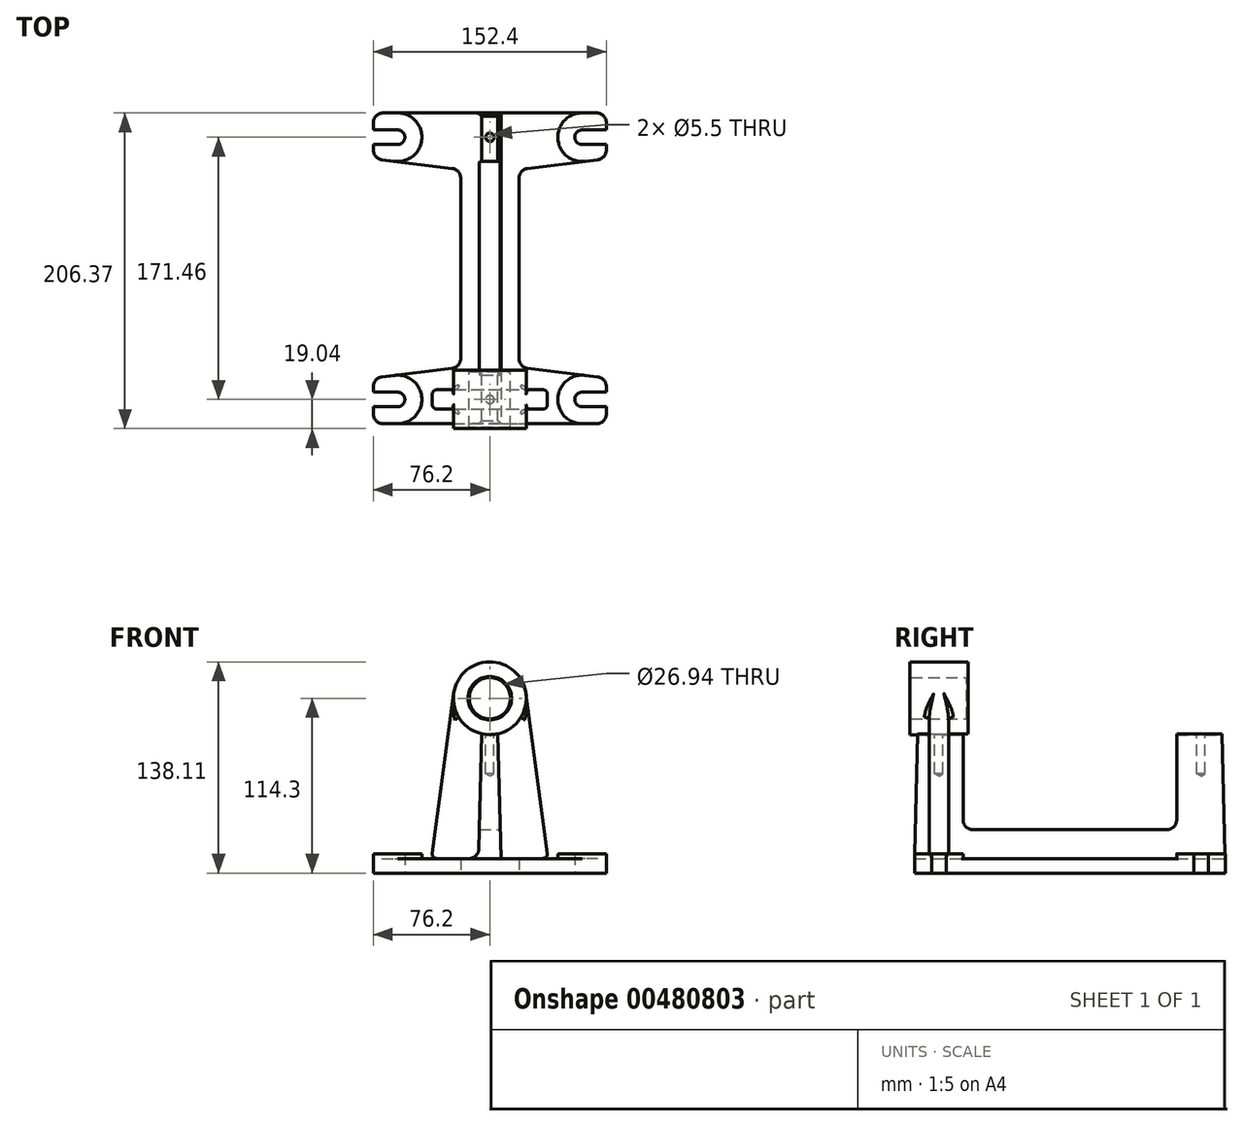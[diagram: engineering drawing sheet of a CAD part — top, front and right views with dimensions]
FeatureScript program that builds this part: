
annotation { "Feature Type Name" : "Feature", "Feature Type Description" : "" }
export const myFeature = defineFeature(function(context is Context, id is Id, definition is map)
    precondition{}
    {
        {
            var Q0;
            Q0=qCreatedBy(makeId("Top.planeOp"),FACE);
            var sketch = newSketch(context, id + "F0", { "sketchPlane" : qUnion([Q0])});
            skLineSegment(sketch, "E0.left", {"start": v(-76.2, 95.25) * mm, "end": v(-76.2, 90.49) * mm});
            skArc(sketch, "E1", {"start": v(-19.05, 59) * mm, "mid": v(-20.64, 63.2) * mm, "end": v(-24.62, 65.3) * mm});
            skLineSegment(sketch, "E2", {"start": v(-70.63, 71) * mm, "end": v(-24.62, 65.3) * mm});
            skArc(sketch, "E3", {"start": v(-60.32, 80.96) * mm, "mid": v(-55.56, 85.72) * mm, "end": v(-60.32, 90.49) * mm});
            skLineSegment(sketch, "E4", {"start": v(-76.2, 90.49) * mm, "end": v(-60.32, 90.49) * mm});
            skLineSegment(sketch, "E5", {"start": v(-60.32, 80.96) * mm, "end": v(-76.2, 80.96) * mm});
            skArc(sketch, "E6.filletArc", {"start": v(-69.85, 101.6) * mm, "mid": v(-74.34, 99.74) * mm, "end": v(-76.2, 95.25) * mm});
            skArc(sketch, "E7.filletArc", {"start": v(-76.2, 77.3) * mm, "mid": v(-74.6, 73.1) * mm, "end": v(-70.63, 71) * mm});
            skLineSegment(sketch, "E8.trimOffspring", {"start": v(-76.2, 80.96) * mm, "end": v(-76.2, 77.3) * mm});
            skLineSegment(sketch, "E9.MirrorCS", {"start": v(76.2, 80.96) * mm, "end": v(76.2, 77.3) * mm});
            skLineSegment(sketch, "E10.MirrorCS", {"start": v(76.2, 95.25) * mm, "end": v(76.2, 90.49) * mm});
            skArc(sketch, "E11.MirrorCS", {"start": v(60.32, 80.96) * mm, "mid": v(55.56, 85.72) * mm, "end": v(60.32, 90.49) * mm});
            skLineSegment(sketch, "E12.MirrorCS", {"start": v(76.2, 90.49) * mm, "end": v(60.32, 90.49) * mm});
            skLineSegment(sketch, "E13.MirrorCS", {"start": v(60.32, 80.96) * mm, "end": v(76.2, 80.96) * mm});
            skArc(sketch, "E14.MirrorCS", {"start": v(69.85, 101.6) * mm, "mid": v(74.34, 99.74) * mm, "end": v(76.2, 95.25) * mm});
            skArc(sketch, "E15.MirrorCS", {"start": v(19.05, 59) * mm, "mid": v(20.64, 63.2) * mm, "end": v(24.62, 65.3) * mm});
            skLineSegment(sketch, "E16.MirrorCS", {"start": v(70.63, 71) * mm, "end": v(24.62, 65.3) * mm});
            skArc(sketch, "E17.MirrorCS", {"start": v(76.2, 77.3) * mm, "mid": v(74.6, 73.1) * mm, "end": v(70.63, 71) * mm});
            skLineSegment(sketch, "E18.MirrorCS", {"start": v(-76.2, -95.25) * mm, "end": v(-76.2, -90.49) * mm});
            skLineSegment(sketch, "E19.MirrorCS", {"start": v(-76.2, -80.96) * mm, "end": v(-76.2, -77.3) * mm});
            skLineSegment(sketch, "E20.MirrorCS", {"start": v(76.2, -95.25) * mm, "end": v(76.2, -90.49) * mm});
            skLineSegment(sketch, "E21.MirrorCS", {"start": v(76.2, -80.96) * mm, "end": v(76.2, -77.3) * mm});
            skArc(sketch, "E22.MirrorCS", {"start": v(-19.05, -59) * mm, "mid": v(-20.64, -63.2) * mm, "end": v(-24.62, -65.3) * mm});
            skArc(sketch, "E23.MirrorCS", {"start": v(-76.2, -77.3) * mm, "mid": v(-74.6, -73.1) * mm, "end": v(-70.63, -71) * mm});
            skLineSegment(sketch, "E24.MirrorCS", {"start": v(-70.63, -71) * mm, "end": v(-24.62, -65.3) * mm});
            skArc(sketch, "E25.MirrorCS", {"start": v(19.05, -59) * mm, "mid": v(20.64, -63.2) * mm, "end": v(24.62, -65.3) * mm});
            skArc(sketch, "E26.MirrorCS", {"start": v(69.85, -101.6) * mm, "mid": v(74.34, -99.74) * mm, "end": v(76.2, -95.25) * mm});
            skLineSegment(sketch, "E27.MirrorCS", {"start": v(60.32, -80.96) * mm, "end": v(76.2, -80.96) * mm});
            skArc(sketch, "E28.MirrorCS", {"start": v(-69.85, -101.6) * mm, "mid": v(-74.34, -99.74) * mm, "end": v(-76.2, -95.25) * mm});
            skLineSegment(sketch, "E29.MirrorCS", {"start": v(-76.2, -90.49) * mm, "end": v(-60.32, -90.49) * mm});
            skArc(sketch, "E30.MirrorCS", {"start": v(-60.32, -80.96) * mm, "mid": v(-55.56, -85.72) * mm, "end": v(-60.32, -90.49) * mm});
            skArc(sketch, "E31.MirrorCS", {"start": v(76.2, -77.3) * mm, "mid": v(74.6, -73.1) * mm, "end": v(70.63, -71) * mm});
            skLineSegment(sketch, "E32.MirrorCS", {"start": v(76.2, -90.49) * mm, "end": v(60.32, -90.49) * mm});
            skLineSegment(sketch, "E33.MirrorCS", {"start": v(-60.32, -80.96) * mm, "end": v(-76.2, -80.96) * mm});
            skLineSegment(sketch, "E34.MirrorCS", {"start": v(70.63, -71) * mm, "end": v(24.62, -65.3) * mm});
            skArc(sketch, "E35.MirrorCS", {"start": v(60.32, -80.96) * mm, "mid": v(55.56, -85.72) * mm, "end": v(60.32, -90.49) * mm});
            skLineSegment(sketch, "E36", {"start": v(-69.85, 101.6) * mm, "end": v(69.85, 101.6) * mm});
            skLineSegment(sketch, "E37", {"start": v(-19.05, 59) * mm, "end": v(-19.05, -59) * mm});
            skLineSegment(sketch, "E38", {"start": v(19.05, 59) * mm, "end": v(19.05, -59) * mm});
            skLineSegment(sketch, "E39", {"start": v(-69.85, -101.6) * mm, "end": v(69.85, -101.6) * mm});
            skSolve(sketch);
        }
        {
            var Q0;
            Q0=makeQuery(id+"F0.imprint","IMPRINT",FACE,{"disambiguationData":[TD([[makeQuery(id+"F0.imprint","IMPRINT",EDGE,{"derivedFrom":sQuery(id+"F0.wireOp",EDGE,"E0.left")}),1.0]])]});
            extrude(context, id + "F1", {"entities" : qUnion([Q0]), "depth" : 9.52 * mm});
        }
        {
            var Q0;
            Q0=makeQuery(id+"F1.opExtrude","CAP_FACE",FACE,{"disambiguationData":[OSD([sQuery(id+"F0.wireOp",EDGE,"E0.left"),sQuery(id+"F0.wireOp",EDGE,"E1"),sQuery(id+"F0.wireOp",EDGE,"E2"),sQuery(id+"F0.wireOp",EDGE,"E3"),sQuery(id+"F0.wireOp",EDGE,"E4"),sQuery(id+"F0.wireOp",EDGE,"E5"),sQuery(id+"F0.wireOp",EDGE,"E6.filletArc"),sQuery(id+"F0.wireOp",EDGE,"E7.filletArc"),sQuery(id+"F0.wireOp",EDGE,"E8.trimOffspring"),sQuery(id+"F0.wireOp",EDGE,"E9.MirrorCS"),sQuery(id+"F0.wireOp",EDGE,"E10.MirrorCS"),sQuery(id+"F0.wireOp",EDGE,"E11.MirrorCS"),sQuery(id+"F0.wireOp",EDGE,"E12.MirrorCS"),sQuery(id+"F0.wireOp",EDGE,"E13.MirrorCS"),sQuery(id+"F0.wireOp",EDGE,"E14.MirrorCS"),sQuery(id+"F0.wireOp",EDGE,"E15.MirrorCS"),sQuery(id+"F0.wireOp",EDGE,"E16.MirrorCS"),sQuery(id+"F0.wireOp",EDGE,"E17.MirrorCS"),sQuery(id+"F0.wireOp",EDGE,"E18.MirrorCS"),sQuery(id+"F0.wireOp",EDGE,"E19.MirrorCS"),sQuery(id+"F0.wireOp",EDGE,"E20.MirrorCS"),sQuery(id+"F0.wireOp",EDGE,"E21.MirrorCS"),sQuery(id+"F0.wireOp",EDGE,"E22.MirrorCS"),sQuery(id+"F0.wireOp",EDGE,"E23.MirrorCS"),sQuery(id+"F0.wireOp",EDGE,"E24.MirrorCS"),sQuery(id+"F0.wireOp",EDGE,"E25.MirrorCS"),sQuery(id+"F0.wireOp",EDGE,"E26.MirrorCS"),sQuery(id+"F0.wireOp",EDGE,"E27.MirrorCS"),sQuery(id+"F0.wireOp",EDGE,"E28.MirrorCS"),sQuery(id+"F0.wireOp",EDGE,"E29.MirrorCS"),sQuery(id+"F0.wireOp",EDGE,"E30.MirrorCS"),sQuery(id+"F0.wireOp",EDGE,"E31.MirrorCS"),sQuery(id+"F0.wireOp",EDGE,"E32.MirrorCS"),sQuery(id+"F0.wireOp",EDGE,"E33.MirrorCS"),sQuery(id+"F0.wireOp",EDGE,"E34.MirrorCS"),sQuery(id+"F0.wireOp",EDGE,"E35.MirrorCS"),sQuery(id+"F0.wireOp",EDGE,"E36"),sQuery(id+"F0.wireOp",EDGE,"E37"),sQuery(id+"F0.wireOp",EDGE,"E38"),sQuery(id+"F0.wireOp",EDGE,"E39")])],"isStart":false});
            var sketch = newSketch(context, id + "F2", { "sketchPlane" : qUnion([Q0])});
            skArc(sketch, "E40", {"start": v(-62.28, 69.97) * mm, "mid": v(-44.48, 84.75) * mm, "end": v(-60.32, 101.6) * mm});
            skLineSegment(sketch, "E41.0", {"start": v(-69.85, 101.6) * mm, "end": v(-60.32, 101.6) * mm});
            skArc(sketch, "E42.0", {"start": v(-69.85, 101.6) * mm, "mid": v(-74.34, 99.74) * mm, "end": v(-76.2, 95.25) * mm});
            skLineSegment(sketch, "E43.0", {"start": v(-76.2, 95.25) * mm, "end": v(-76.2, 90.49) * mm});
            skLineSegment(sketch, "E44.0", {"start": v(-76.2, 80.96) * mm, "end": v(-76.2, 77.3) * mm});
            skArc(sketch, "E45.0", {"start": v(-76.2, 77.3) * mm, "mid": v(-74.6, 73.1) * mm, "end": v(-70.63, 71) * mm});
            skLineSegment(sketch, "E46.0", {"start": v(-70.63, 71) * mm, "end": v(-62.28, 69.97) * mm});
            skLineSegment(sketch, "E47.0", {"start": v(-76.2, 90.49) * mm, "end": v(-60.32, 90.49) * mm});
            skArc(sketch, "E48.0", {"start": v(-60.32, 80.96) * mm, "mid": v(-55.56, 85.72) * mm, "end": v(-60.32, 90.49) * mm});
            skLineSegment(sketch, "E49.0", {"start": v(-60.32, 80.96) * mm, "end": v(-76.2, 80.96) * mm});
            skLineSegment(sketch, "E50.MirrorCS", {"start": v(76.2, 80.96) * mm, "end": v(76.2, 77.3) * mm});
            skLineSegment(sketch, "E51.MirrorCS", {"start": v(76.2, 95.25) * mm, "end": v(76.2, 90.49) * mm});
            skLineSegment(sketch, "E52.MirrorCS", {"start": v(70.63, 71) * mm, "end": v(62.28, 69.97) * mm});
            skLineSegment(sketch, "E53.MirrorCS", {"start": v(76.2, 90.49) * mm, "end": v(60.32, 90.49) * mm});
            skArc(sketch, "E54.MirrorCS", {"start": v(76.2, 77.3) * mm, "mid": v(74.6, 73.1) * mm, "end": v(70.63, 71) * mm});
            skArc(sketch, "E55.MirrorCS", {"start": v(60.32, 80.96) * mm, "mid": v(55.56, 85.72) * mm, "end": v(60.32, 90.49) * mm});
            skLineSegment(sketch, "E56.MirrorCS", {"start": v(60.32, 80.96) * mm, "end": v(76.2, 80.96) * mm});
            skArc(sketch, "E57.MirrorCS", {"start": v(69.85, 101.6) * mm, "mid": v(74.34, 99.74) * mm, "end": v(76.2, 95.25) * mm});
            skLineSegment(sketch, "E58.MirrorCS", {"start": v(69.85, 101.6) * mm, "end": v(60.32, 101.6) * mm});
            skArc(sketch, "E59.MirrorCS", {"start": v(62.28, 69.97) * mm, "mid": v(44.48, 84.75) * mm, "end": v(60.32, 101.6) * mm});
            skLineSegment(sketch, "E60.MirrorCS", {"start": v(-76.2, -80.96) * mm, "end": v(-76.2, -77.3) * mm});
            skLineSegment(sketch, "E61.MirrorCS", {"start": v(-76.2, -95.25) * mm, "end": v(-76.2, -90.49) * mm});
            skLineSegment(sketch, "E62.MirrorCS", {"start": v(76.2, -80.96) * mm, "end": v(76.2, -77.3) * mm});
            skLineSegment(sketch, "E63.MirrorCS", {"start": v(76.2, -95.25) * mm, "end": v(76.2, -90.49) * mm});
            skLineSegment(sketch, "E64.MirrorCS", {"start": v(-70.63, -71) * mm, "end": v(-62.28, -69.97) * mm});
            skArc(sketch, "E65.MirrorCS", {"start": v(-76.2, -77.3) * mm, "mid": v(-74.6, -73.1) * mm, "end": v(-70.63, -71) * mm});
            skArc(sketch, "E66.MirrorCS", {"start": v(-69.85, -101.6) * mm, "mid": v(-74.34, -99.74) * mm, "end": v(-76.2, -95.25) * mm});
            skLineSegment(sketch, "E67.MirrorCS", {"start": v(-69.85, -101.6) * mm, "end": v(-60.32, -101.6) * mm});
            skArc(sketch, "E68.MirrorCS", {"start": v(-62.28, -69.97) * mm, "mid": v(-44.48, -84.75) * mm, "end": v(-60.32, -101.6) * mm});
            skArc(sketch, "E69.MirrorCS", {"start": v(60.32, -80.96) * mm, "mid": v(55.56, -85.72) * mm, "end": v(60.32, -90.49) * mm});
            skArc(sketch, "E70.MirrorCS", {"start": v(76.2, -77.3) * mm, "mid": v(74.6, -73.1) * mm, "end": v(70.63, -71) * mm});
            skLineSegment(sketch, "E71.MirrorCS", {"start": v(76.2, -90.49) * mm, "end": v(60.32, -90.49) * mm});
            skLineSegment(sketch, "E72.MirrorCS", {"start": v(-76.2, -90.49) * mm, "end": v(-60.32, -90.49) * mm});
            skArc(sketch, "E73.MirrorCS", {"start": v(-60.32, -80.96) * mm, "mid": v(-55.56, -85.72) * mm, "end": v(-60.32, -90.49) * mm});
            skLineSegment(sketch, "E74.MirrorCS", {"start": v(-60.32, -80.96) * mm, "end": v(-76.2, -80.96) * mm});
            skLineSegment(sketch, "E75.MirrorCS", {"start": v(70.63, -71) * mm, "end": v(62.28, -69.97) * mm});
            skArc(sketch, "E76.MirrorCS", {"start": v(69.85, -101.6) * mm, "mid": v(74.34, -99.74) * mm, "end": v(76.2, -95.25) * mm});
            skArc(sketch, "E77.MirrorCS", {"start": v(62.28, -69.97) * mm, "mid": v(44.48, -84.75) * mm, "end": v(60.32, -101.6) * mm});
            skLineSegment(sketch, "E78.MirrorCS", {"start": v(60.32, -80.96) * mm, "end": v(76.2, -80.96) * mm});
            skLineSegment(sketch, "E79.MirrorCS", {"start": v(69.85, -101.6) * mm, "end": v(60.32, -101.6) * mm});
            skSolve(sketch);
        }
        {
            var Q0;
            Q0=makeQuery(id+"F2.imprint","IMPRINT",FACE,{"disambiguationData":[TD([[makeQuery(id+"F2.imprint","IMPRINT",EDGE,{"derivedFrom":sQuery(id+"F2.wireOp",EDGE,"E60.MirrorCS")}),-1.0]])]});
            var Q1;
            Q1=makeQuery(id+"F2.imprint","IMPRINT",FACE,{"disambiguationData":[TD([[makeQuery(id+"F2.imprint","IMPRINT",EDGE,{"derivedFrom":sQuery(id+"F2.wireOp",EDGE,"E62.MirrorCS")}),1.0]])]});
            var Q2;
            Q2=makeQuery(id+"F2.imprint","IMPRINT",FACE,{"disambiguationData":[TD([[makeQuery(id+"F2.imprint","IMPRINT",EDGE,{"derivedFrom":sQuery(id+"F2.wireOp",EDGE,"E40")}),1.0]])]});
            var Q3;
            Q3=makeQuery(id+"F2.imprint","IMPRINT",FACE,{"disambiguationData":[TD([[makeQuery(id+"F2.imprint","IMPRINT",EDGE,{"derivedFrom":sQuery(id+"F2.wireOp",EDGE,"E50.MirrorCS")}),-1.0]])]});
            extrude(context, id + "F3", {"entities" : qUnion([Q0, Q1, Q2, Q3]), "operationType" : NewBodyOperationType.ADD, "depth" : 3.17 * mm});
        }
        {
            var Q0;
            Q0=makeQuery(id+"F3.boolean.opBoolean","MERGE",FACE,{"derivedFrom":[makeQuery(id+"F1.opExtrude","SWEPT_FACE",FACE,{"disambiguationData":[OSD([sQuery(id+"F0.wireOp",EDGE,"E39")])]}),makeQuery(id+"F3.opExtrude","SWEPT_FACE",FACE,{"disambiguationData":[OSD([sQuery(id+"F2.wireOp",EDGE,"E67.MirrorCS")])]}),makeQuery(id+"F3.opExtrude","SWEPT_FACE",FACE,{"disambiguationData":[OSD([sQuery(id+"F2.wireOp",EDGE,"E79.MirrorCS")])]})]});
            cPlane(context, id + "F4", {"entities" : qUnion([Q0]), "cplaneType" : CPlaneType.OFFSET, "offset" : 15.88 * mm, "oppositeDirection" : true, "width" : 152.4 * mm, "height" : 152.4 * mm});
        }
        {
            var Q0;
            Q0=qCreatedBy(id+"F4.planeOp",FACE);
            var sketch = newSketch(context, id + "F5", { "sketchPlane" : qUnion([Q0])});
            skCircle(sketch, "E80", {"center": v(0, 114.3) * mm, "radius": 23.81 * mm});
            skCircle(sketch, "E81", {"center": v(0, 114.3) * mm, "radius": 13.47 * mm});
            skSolve(sketch);
        }
        {
            var Q0;
            Q0=makeQuery(id+"F5.imprint","IMPRINT",FACE,{"disambiguationData":[TD([[makeQuery(id+"F5.imprint","IMPRINT",EDGE,{"derivedFrom":sQuery(id+"F5.wireOp",EDGE,"E80")}),1.0]])]});
            extrude(context, id + "F6", {"entities" : qUnion([Q0]), "endBound" : BoundingType.SYMMETRIC, "depth" : 38.1 * mm});
        }
        {
            var Q0;
            Q0=qCreatedBy(id+"F4.planeOp",FACE);
            var sketch = newSketch(context, id + "F7", { "sketchPlane" : qUnion([Q0])});
            skLineSegment(sketch, "E82", {"start": v(-23.6, 117.47) * mm, "end": v(-38.1, 9.52) * mm});
            skLineSegment(sketch, "E83", {"start": v(38.1, 9.52) * mm, "end": v(23.6, 117.47) * mm});
            skArc(sketch, "E84.0", {"start": v(-23.6, 117.47) * mm, "mid": v(0, 90.49) * mm, "end": v(23.6, 117.47) * mm});
            skLineSegment(sketch, "E85.0", {"start": v(-38.1, 9.53) * mm, "end": v(38.1, 9.53) * mm});
            skSolve(sketch);
        }
        {
            var Q0;
            Q0=makeQuery(id+"F7.imprint","IMPRINT",FACE,{"disambiguationData":[TD([[makeQuery(id+"F7.imprint","IMPRINT",EDGE,{"derivedFrom":sQuery(id+"F7.wireOp",EDGE,"E82")}),1.0]])]});
            extrude(context, id + "F8", {"entities" : qUnion([Q0]), "operationType" : NewBodyOperationType.ADD, "endBound" : BoundingType.SYMMETRIC, "depth" : 12.7 * mm});
        }
        {
            var Q0;
            Q0=makeQuery(id+"F1.opExtrude","CAP_FACE",FACE,{"disambiguationData":[OSD([sQuery(id+"F0.wireOp",EDGE,"E0.left"),sQuery(id+"F0.wireOp",EDGE,"E1"),sQuery(id+"F0.wireOp",EDGE,"E2"),sQuery(id+"F0.wireOp",EDGE,"E3"),sQuery(id+"F0.wireOp",EDGE,"E4"),sQuery(id+"F0.wireOp",EDGE,"E5"),sQuery(id+"F0.wireOp",EDGE,"E6.filletArc"),sQuery(id+"F0.wireOp",EDGE,"E7.filletArc"),sQuery(id+"F0.wireOp",EDGE,"E8.trimOffspring"),sQuery(id+"F0.wireOp",EDGE,"E9.MirrorCS"),sQuery(id+"F0.wireOp",EDGE,"E10.MirrorCS"),sQuery(id+"F0.wireOp",EDGE,"E11.MirrorCS"),sQuery(id+"F0.wireOp",EDGE,"E12.MirrorCS"),sQuery(id+"F0.wireOp",EDGE,"E13.MirrorCS"),sQuery(id+"F0.wireOp",EDGE,"E14.MirrorCS"),sQuery(id+"F0.wireOp",EDGE,"E15.MirrorCS"),sQuery(id+"F0.wireOp",EDGE,"E16.MirrorCS"),sQuery(id+"F0.wireOp",EDGE,"E17.MirrorCS"),sQuery(id+"F0.wireOp",EDGE,"E18.MirrorCS"),sQuery(id+"F0.wireOp",EDGE,"E19.MirrorCS"),sQuery(id+"F0.wireOp",EDGE,"E20.MirrorCS"),sQuery(id+"F0.wireOp",EDGE,"E21.MirrorCS"),sQuery(id+"F0.wireOp",EDGE,"E22.MirrorCS"),sQuery(id+"F0.wireOp",EDGE,"E23.MirrorCS"),sQuery(id+"F0.wireOp",EDGE,"E24.MirrorCS"),sQuery(id+"F0.wireOp",EDGE,"E25.MirrorCS"),sQuery(id+"F0.wireOp",EDGE,"E26.MirrorCS"),sQuery(id+"F0.wireOp",EDGE,"E27.MirrorCS"),sQuery(id+"F0.wireOp",EDGE,"E28.MirrorCS"),sQuery(id+"F0.wireOp",EDGE,"E29.MirrorCS"),sQuery(id+"F0.wireOp",EDGE,"E30.MirrorCS"),sQuery(id+"F0.wireOp",EDGE,"E31.MirrorCS"),sQuery(id+"F0.wireOp",EDGE,"E32.MirrorCS"),sQuery(id+"F0.wireOp",EDGE,"E33.MirrorCS"),sQuery(id+"F0.wireOp",EDGE,"E34.MirrorCS"),sQuery(id+"F0.wireOp",EDGE,"E35.MirrorCS"),sQuery(id+"F0.wireOp",EDGE,"E36"),sQuery(id+"F0.wireOp",EDGE,"E37"),sQuery(id+"F0.wireOp",EDGE,"E38"),sQuery(id+"F0.wireOp",EDGE,"E39")])],"isStart":false});
            var sketch = newSketch(context, id + "F9", { "sketchPlane" : qUnion([Q0])});
            skLineSegment(sketch, "E86.left", {"start": v(-7.35, 101.6) * mm, "end": v(-7.35, -101.6) * mm});
            skLineSegment(sketch, "E86.right", {"start": v(7.35, 101.6) * mm, "end": v(7.35, -101.6) * mm});
            skLineSegment(sketch, "E87", {"start": v(7.35, -101.6) * mm, "end": v(-7.35, -101.6) * mm});
            skLineSegment(sketch, "E88", {"start": v(-7.35, 101.6) * mm, "end": v(7.35, 101.6) * mm});
            skSolve(sketch);
        }
        {
            var Q0;
            Q0=makeQuery(id+"F9.imprint","IMPRINT",FACE,{"disambiguationData":[TD([[makeQuery(id+"F9.imprint","IMPRINT",EDGE,{"derivedFrom":sQuery(id+"F9.wireOp",EDGE,"E86.left")}),1.0]])]});
            var Q1;
            Q1=makeQuery(id+"F6.opExtrude","SWEPT_FACE",FACE,{"disambiguationData":[OSD([sQuery(id+"F5.wireOp",EDGE,"E80")])]});
            extrude(context, id + "F10", {"entities" : qUnion([Q0]), "endBound" : BoundingType.UP_TO_SURFACE, "endBoundEntityFace" : qUnion([Q1]), "depth" : 25.4 * mm, "hasDraft" : true, "draftAngle" : 1.5 * degree, "draftPullDirection" : true});
        }
        {
            var Q0;
            Q0=qCreatedBy(makeId("Right.planeOp"),FACE);
            var sketch = newSketch(context, id + "F11", { "sketchPlane" : qUnion([Q0])});
            skLineSegment(sketch, "E89.MirrorCS", {"start": v(69.85, 91.1) * mm, "end": v(69.85, 34.77) * mm});
            skLineSegment(sketch, "E90.MirrorCS", {"start": v(-69.85, 91.1) * mm, "end": v(-69.85, 34.77) * mm});
            skLineSegment(sketch, "E91.0", {"start": v(63.5, 28.42) * mm, "end": v(-63.5, 28.42) * mm});
            skPoint(sketch, "E92.newPointA", {"position": v(69.85, 9.52) * mm});
            skArc(sketch, "E92.filletArc", {"start": v(63.5, 28.42) * mm, "mid": v(68, 30.28) * mm, "end": v(69.85, 34.77) * mm});
            skPoint(sketch, "E93.newPointB", {"position": v(-69.85, 9.52) * mm});
            skArc(sketch, "E93.filletArc", {"start": v(-69.85, 34.77) * mm, "mid": v(-68, 30.28) * mm, "end": v(-63.5, 28.42) * mm});
            skLineSegment(sketch, "E94", {"start": v(69.85, 91.1) * mm, "end": v(-69.85, 91.1) * mm});
            skSolve(sketch);
        }
        {
            var Q0;
            Q0=makeQuery(id+"F11.imprint","IMPRINT",FACE,{"disambiguationData":[TD([[makeQuery(id+"F11.imprint","IMPRINT",EDGE,{"derivedFrom":sQuery(id+"F11.wireOp",EDGE,"E89.MirrorCS")}),-1.0]])]});
            extrude(context, id + "F12", {"entities" : qUnion([Q0]), "operationType" : NewBodyOperationType.REMOVE, "endBound" : BoundingType.SYMMETRIC, "oppositeDirection" : true, "depth" : 50.8 * mm});
        }
        {
            var Q0;
            Q0=makeQuery(id+"F10.opExtrude","SWEPT_BODY",BODY,{"disambiguationData":[OSD([sQuery(id+"F9.wireOp",EDGE,"E86.left"),sQuery(id+"F9.wireOp",EDGE,"E86.right"),sQuery(id+"F9.wireOp",EDGE,"E87"),sQuery(id+"F9.wireOp",EDGE,"E88")])]});
            var Q1;
            Q1=makeQuery(id+"F1.opExtrude","SWEPT_BODY",BODY,{"disambiguationData":[OSD([sQuery(id+"F0.wireOp",EDGE,"E0.left"),sQuery(id+"F0.wireOp",EDGE,"E1"),sQuery(id+"F0.wireOp",EDGE,"E2"),sQuery(id+"F0.wireOp",EDGE,"E3"),sQuery(id+"F0.wireOp",EDGE,"E4"),sQuery(id+"F0.wireOp",EDGE,"E5"),sQuery(id+"F0.wireOp",EDGE,"E6.filletArc"),sQuery(id+"F0.wireOp",EDGE,"E7.filletArc"),sQuery(id+"F0.wireOp",EDGE,"E8.trimOffspring"),sQuery(id+"F0.wireOp",EDGE,"E9.MirrorCS"),sQuery(id+"F0.wireOp",EDGE,"E10.MirrorCS"),sQuery(id+"F0.wireOp",EDGE,"E11.MirrorCS"),sQuery(id+"F0.wireOp",EDGE,"E12.MirrorCS"),sQuery(id+"F0.wireOp",EDGE,"E13.MirrorCS"),sQuery(id+"F0.wireOp",EDGE,"E14.MirrorCS"),sQuery(id+"F0.wireOp",EDGE,"E15.MirrorCS"),sQuery(id+"F0.wireOp",EDGE,"E16.MirrorCS"),sQuery(id+"F0.wireOp",EDGE,"E17.MirrorCS"),sQuery(id+"F0.wireOp",EDGE,"E18.MirrorCS"),sQuery(id+"F0.wireOp",EDGE,"E19.MirrorCS"),sQuery(id+"F0.wireOp",EDGE,"E20.MirrorCS"),sQuery(id+"F0.wireOp",EDGE,"E21.MirrorCS"),sQuery(id+"F0.wireOp",EDGE,"E22.MirrorCS"),sQuery(id+"F0.wireOp",EDGE,"E23.MirrorCS"),sQuery(id+"F0.wireOp",EDGE,"E24.MirrorCS"),sQuery(id+"F0.wireOp",EDGE,"E25.MirrorCS"),sQuery(id+"F0.wireOp",EDGE,"E26.MirrorCS"),sQuery(id+"F0.wireOp",EDGE,"E27.MirrorCS"),sQuery(id+"F0.wireOp",EDGE,"E28.MirrorCS"),sQuery(id+"F0.wireOp",EDGE,"E29.MirrorCS"),sQuery(id+"F0.wireOp",EDGE,"E30.MirrorCS"),sQuery(id+"F0.wireOp",EDGE,"E31.MirrorCS"),sQuery(id+"F0.wireOp",EDGE,"E32.MirrorCS"),sQuery(id+"F0.wireOp",EDGE,"E33.MirrorCS"),sQuery(id+"F0.wireOp",EDGE,"E34.MirrorCS"),sQuery(id+"F0.wireOp",EDGE,"E35.MirrorCS"),sQuery(id+"F0.wireOp",EDGE,"E36"),sQuery(id+"F0.wireOp",EDGE,"E37"),sQuery(id+"F0.wireOp",EDGE,"E38"),sQuery(id+"F0.wireOp",EDGE,"E39")])]});
            booleanBodies(context, id + "F13", {"operationType" : BooleanOperationType.UNION, "tools" : qUnion([Q0, Q1])});
        }
        {
            var Q0;
            {var subQ0=sQuery(id+"F7.wireOp",EDGE,"E85.0");var subQ1=sQuery(id+"F7.wireOp",EDGE,"E84.0");var subQ2=sQuery(id+"F7.wireOp",EDGE,"E83");var subQ3=sQuery(id+"F7.wireOp",EDGE,"E82");var subQ4=sQuery(id+"F9.wireOp",EDGE,"E86.right");Q0=makeQuery(id+"F13.opBoolean","SPLIT",EDGE,{"disambiguationData":[TD([makeQuery(id+"F8.opExtrude","CAP_FACE",FACE,{"disambiguationData":[OSD([subQ3,subQ2,subQ1,subQ0])],"isStart":true})])],"derivedFrom":makeQuery(id+"F10.opExtrude","CAP_EDGE",EDGE,{"disambiguationData":[OSD([subQ4])],"isStart":true})});}
            var Q1;
            {var subQ0=sQuery(id+"F9.wireOp",EDGE,"E86.left");var subQ1=sQuery(id+"F7.wireOp",EDGE,"E85.0");var subQ2=sQuery(id+"F7.wireOp",EDGE,"E84.0");var subQ3=sQuery(id+"F7.wireOp",EDGE,"E83");var subQ4=sQuery(id+"F7.wireOp",EDGE,"E82");Q1=makeQuery(id+"F13.opBoolean","SPLIT",EDGE,{"disambiguationData":[TD([makeQuery(id+"F8.opExtrude","CAP_FACE",FACE,{"disambiguationData":[OSD([subQ4,subQ3,subQ2,subQ1])],"isStart":true})])],"derivedFrom":makeQuery(id+"F10.opExtrude","CAP_EDGE",EDGE,{"disambiguationData":[OSD([subQ0])],"isStart":true})});}
            fillet(context, id + "F14", {"entities" : qUnion([Q0, Q1]), "radius" : 6.35 * mm, "tangentPropagation" : true, "allowEdgeOverflow" : false});
        }
        {
            var Q0;
            {var subQ0=sQuery(id+"F9.wireOp",EDGE,"E86.left");var subQ1=sQuery(id+"F0.wireOp",EDGE,"E39");Q0=makeQuery(id+"F13.opBoolean","SPLIT",EDGE,{"disambiguationData":[TD([makeQuery(id+"F1.opExtrude","SWEPT_FACE",FACE,{"disambiguationData":[OSD([subQ1])]})])],"derivedFrom":makeQuery(id+"F10.opExtrude","CAP_EDGE",EDGE,{"disambiguationData":[OSD([subQ0])],"isStart":true})});}
            var Q1;
            {var subQ0=sQuery(id+"F0.wireOp",EDGE,"E39");var subQ1=sQuery(id+"F9.wireOp",EDGE,"E86.right");Q1=makeQuery(id+"F13.opBoolean","SPLIT",EDGE,{"disambiguationData":[TD([makeQuery(id+"F1.opExtrude","SWEPT_FACE",FACE,{"disambiguationData":[OSD([subQ0])]})])],"derivedFrom":makeQuery(id+"F10.opExtrude","CAP_EDGE",EDGE,{"disambiguationData":[OSD([subQ1])],"isStart":true})});}
            var Q2;
            {var subQ0=sQuery(id+"F0.wireOp",EDGE,"E36");var subQ1=sQuery(id+"F9.wireOp",EDGE,"E86.right");Q2=makeQuery(id+"F13.opBoolean","SPLIT",EDGE,{"disambiguationData":[TD([makeQuery(id+"F1.opExtrude","SWEPT_FACE",FACE,{"disambiguationData":[OSD([subQ0])]})])],"derivedFrom":makeQuery(id+"F10.opExtrude","CAP_EDGE",EDGE,{"disambiguationData":[OSD([subQ1])],"isStart":true})});}
            var Q3;
            {var subQ0=sQuery(id+"F9.wireOp",EDGE,"E86.left");var subQ1=sQuery(id+"F0.wireOp",EDGE,"E36");Q3=makeQuery(id+"F13.opBoolean","SPLIT",EDGE,{"disambiguationData":[TD([makeQuery(id+"F1.opExtrude","SWEPT_FACE",FACE,{"disambiguationData":[OSD([subQ1])]})])],"derivedFrom":makeQuery(id+"F10.opExtrude","CAP_EDGE",EDGE,{"disambiguationData":[OSD([subQ0])],"isStart":true})});}
            var Q4;
            {var subQ0=sQuery(id+"F7.wireOp",EDGE,"E82");Q4=makeQuery(id+"F13.opBoolean","SPLIT",FACE,{"disambiguationData":[TD([makeQuery(id+"F8.opExtrude","SWEPT_FACE",FACE,{"disambiguationData":[OSD([subQ0])]})])],"derivedFrom":makeQuery(id+"F8.opExtrude","CAP_FACE",FACE,{"disambiguationData":[OSD([subQ0,sQuery(id+"F7.wireOp",EDGE,"E83"),sQuery(id+"F7.wireOp",EDGE,"E84.0"),sQuery(id+"F7.wireOp",EDGE,"E85.0")])],"isStart":true})});}
            var Q5;
            {var subQ0=sQuery(id+"F7.wireOp",EDGE,"E83");Q5=makeQuery(id+"F13.opBoolean","SPLIT",FACE,{"disambiguationData":[TD([makeQuery(id+"F8.opExtrude","SWEPT_FACE",FACE,{"disambiguationData":[OSD([subQ0])]})])],"derivedFrom":makeQuery(id+"F8.opExtrude","CAP_FACE",FACE,{"disambiguationData":[OSD([sQuery(id+"F7.wireOp",EDGE,"E82"),subQ0,sQuery(id+"F7.wireOp",EDGE,"E84.0"),sQuery(id+"F7.wireOp",EDGE,"E85.0")])],"isStart":true})});}
            var Q6;
            Q6=makeQuery(id+"F8.opExtrude","SWEPT_FACE",FACE,{"disambiguationData":[OSD([sQuery(id+"F7.wireOp",EDGE,"E83")])]});
            var Q7;
            {var subQ0=sQuery(id+"F7.wireOp",EDGE,"E83");Q7=makeQuery(id+"F13.opBoolean","SPLIT",FACE,{"disambiguationData":[TD([makeQuery(id+"F8.opExtrude","SWEPT_FACE",FACE,{"disambiguationData":[OSD([subQ0])]})])],"derivedFrom":makeQuery(id+"F8.opExtrude","CAP_FACE",FACE,{"disambiguationData":[OSD([sQuery(id+"F7.wireOp",EDGE,"E82"),subQ0,sQuery(id+"F7.wireOp",EDGE,"E84.0"),sQuery(id+"F7.wireOp",EDGE,"E85.0")])],"isStart":false})});}
            var Q8;
            {var subQ0=sQuery(id+"F7.wireOp",EDGE,"E82");Q8=makeQuery(id+"F13.opBoolean","SPLIT",FACE,{"disambiguationData":[TD([makeQuery(id+"F8.opExtrude","SWEPT_FACE",FACE,{"disambiguationData":[OSD([subQ0])]})])],"derivedFrom":makeQuery(id+"F8.opExtrude","CAP_FACE",FACE,{"disambiguationData":[OSD([subQ0,sQuery(id+"F7.wireOp",EDGE,"E83"),sQuery(id+"F7.wireOp",EDGE,"E84.0"),sQuery(id+"F7.wireOp",EDGE,"E85.0")])],"isStart":false})});}
            var Q9;
            Q9=makeQuery(id+"F8.opExtrude","SWEPT_FACE",FACE,{"disambiguationData":[OSD([sQuery(id+"F7.wireOp",EDGE,"E82")])]});
            var Q10;
            Q10=makeQuery(id+"F10.opExtrude","SWEPT_EDGE",EDGE,{"disambiguationData":[OSD([sQuery(id+"F0.wireOp",EDGE,"E39"),sQuery(id+"F9.wireOp",EDGE,"E86.left"),sQuery(id+"F9.wireOp",EDGE,"E87")])]});
            var Q11;
            {var subQ0=sQuery(id+"F0.wireOp",EDGE,"E39");Q11=makeQuery(id+"F13.opBoolean","SPLIT",EDGE,{"disambiguationData":[TD([makeQuery(id+"F3.opExtrude","SWEPT_FACE",FACE,{"disambiguationData":[OSD([sQuery(id+"F2.wireOp",EDGE,"E68.MirrorCS")])]})])],"derivedFrom":makeQuery(id+"F1.opExtrude","CAP_EDGE",EDGE,{"disambiguationData":[OSD([subQ0])],"isStart":false})});}
            var Q12;
            Q12=makeQuery(id+"F10.opExtrude","SWEPT_EDGE",EDGE,{"disambiguationData":[OSD([sQuery(id+"F0.wireOp",EDGE,"E39"),sQuery(id+"F9.wireOp",EDGE,"E86.right"),sQuery(id+"F9.wireOp",EDGE,"E87")])]});
            var Q13;
            {var subQ0=sQuery(id+"F0.wireOp",EDGE,"E39");Q13=makeQuery(id+"F13.opBoolean","SPLIT",EDGE,{"disambiguationData":[TD([makeQuery(id+"F3.opExtrude","SWEPT_FACE",FACE,{"disambiguationData":[OSD([sQuery(id+"F2.wireOp",EDGE,"E77.MirrorCS")])]})])],"derivedFrom":makeQuery(id+"F1.opExtrude","CAP_EDGE",EDGE,{"disambiguationData":[OSD([subQ0])],"isStart":false})});}
            var Q14;
            Q14=makeQuery(id+"F12.boolean.opBoolean","INTERSECT",EDGE,{"derivedFrom":[makeQuery(id+"F10.opExtrude","SWEPT_FACE",FACE,{"disambiguationData":[OSD([sQuery(id+"F9.wireOp",EDGE,"E86.left")])]}),makeQuery(id+"F12.opExtrude","SWEPT_FACE",FACE,{"disambiguationData":[OSD([sQuery(id+"F11.wireOp",EDGE,"E90.MirrorCS")])]})]});
            var Q15;
            Q15=makeQuery(id+"F12.boolean.opBoolean","INTERSECT",EDGE,{"derivedFrom":[makeQuery(id+"F10.opExtrude","SWEPT_FACE",FACE,{"disambiguationData":[OSD([sQuery(id+"F9.wireOp",EDGE,"E86.left")])]}),makeQuery(id+"F12.opExtrude","SWEPT_FACE",FACE,{"disambiguationData":[OSD([sQuery(id+"F11.wireOp",EDGE,"E93.filletArc")])]})]});
            var Q16;
            Q16=makeQuery(id+"F12.boolean.opBoolean","INTERSECT",EDGE,{"derivedFrom":[makeQuery(id+"F10.opExtrude","SWEPT_FACE",FACE,{"disambiguationData":[OSD([sQuery(id+"F9.wireOp",EDGE,"E86.right")])]}),makeQuery(id+"F12.opExtrude","SWEPT_FACE",FACE,{"disambiguationData":[OSD([sQuery(id+"F11.wireOp",EDGE,"E91.0")])]})]});
            var Q17;
            Q17=makeQuery(id+"F12.boolean.opBoolean","INTERSECT",EDGE,{"derivedFrom":[makeQuery(id+"F10.opExtrude","SWEPT_FACE",FACE,{"disambiguationData":[OSD([sQuery(id+"F9.wireOp",EDGE,"E86.right")])]}),makeQuery(id+"F12.opExtrude","SWEPT_FACE",FACE,{"disambiguationData":[OSD([sQuery(id+"F11.wireOp",EDGE,"E93.filletArc")])]})]});
            var Q18;
            Q18=makeQuery(id+"F12.boolean.opBoolean","INTERSECT",EDGE,{"derivedFrom":[makeQuery(id+"F10.opExtrude","CAP_FACE",FACE,{"disambiguationData":[OSD([sQuery(id+"F5.wireOp",EDGE,"E80")])],"isStart":false}),makeQuery(id+"F12.opExtrude","SWEPT_FACE",FACE,{"disambiguationData":[OSD([sQuery(id+"F11.wireOp",EDGE,"E90.MirrorCS")])]})]});
            var Q19;
            {var subQ0=sQuery(id+"F7.wireOp",EDGE,"E82");Q19=makeQuery(id+"F13.opBoolean","SPLIT",FACE,{"disambiguationData":[TD([makeQuery(id+"F4iPU1aoNzSSLv7_1.1.F8.opExtrude","SWEPT_FACE",FACE,{"disambiguationData":[OSD([subQ0])]})])],"derivedFrom":makeQuery(id+"F4iPU1aoNzSSLv7_1.1.F8.opExtrude","CAP_FACE",FACE,{"disambiguationData":[OSD([subQ0,sQuery(id+"F7.wireOp",EDGE,"E83"),sQuery(id+"F7.wireOp",EDGE,"E84.0"),sQuery(id+"F7.wireOp",EDGE,"E85.0")])],"isStart":true})});}
            var Q20;
            Q20=makeQuery(id+"F4iPU1aoNzSSLv7_1.1.F8.opExtrude","SWEPT_FACE",FACE,{"disambiguationData":[OSD([sQuery(id+"F7.wireOp",EDGE,"E82")])]});
            var Q21;
            {var subQ0=sQuery(id+"F7.wireOp",EDGE,"E82");Q21=makeQuery(id+"F13.opBoolean","SPLIT",FACE,{"disambiguationData":[TD([makeQuery(id+"F4iPU1aoNzSSLv7_1.1.F8.opExtrude","SWEPT_FACE",FACE,{"disambiguationData":[OSD([subQ0])]})])],"derivedFrom":makeQuery(id+"F4iPU1aoNzSSLv7_1.1.F8.opExtrude","CAP_FACE",FACE,{"disambiguationData":[OSD([subQ0,sQuery(id+"F7.wireOp",EDGE,"E83"),sQuery(id+"F7.wireOp",EDGE,"E84.0"),sQuery(id+"F7.wireOp",EDGE,"E85.0")])],"isStart":false})});}
            var Q22;
            {var subQ0=sQuery(id+"F0.wireOp",EDGE,"E36");Q22=makeQuery(id+"F13.opBoolean","SPLIT",FACE,{"disambiguationData":[TD([makeQuery(id+"F1.opExtrude","SWEPT_FACE",FACE,{"disambiguationData":[OSD([subQ0])]})])],"derivedFrom":makeQuery(id+"F10.opExtrude","SWEPT_FACE",FACE,{"disambiguationData":[OSD([sQuery(id+"F9.wireOp",EDGE,"E86.left")])]})});}
            var Q23;
            {var subQ4=sQuery(id+"F0.wireOp",EDGE,"E24.MirrorCS");var subQ5=sQuery(id+"F0.wireOp",EDGE,"E22.MirrorCS");var subQ6=sQuery(id+"F0.wireOp",EDGE,"E1");var subQ7=sQuery(id+"F0.wireOp",EDGE,"E36");var subQ8=sQuery(id+"F0.wireOp",EDGE,"E37");var subQ9=sQuery(id+"F0.wireOp",EDGE,"E39");var subQ10=sQuery(id+"F0.wireOp",EDGE,"E2");Q23=makeQuery(id+"F13.opBoolean","SPLIT",FACE,{"disambiguationData":[TD([makeQuery(id+"F1.opExtrude","SWEPT_FACE",FACE,{"disambiguationData":[OSD([subQ6])]})])],"derivedFrom":makeQuery(id+"F1.opExtrude","CAP_FACE",FACE,{"disambiguationData":[OSD([sQuery(id+"F0.wireOp",EDGE,"E0.left"),subQ6,subQ10,sQuery(id+"F0.wireOp",EDGE,"E3"),sQuery(id+"F0.wireOp",EDGE,"E4"),sQuery(id+"F0.wireOp",EDGE,"E5"),sQuery(id+"F0.wireOp",EDGE,"E6.filletArc"),sQuery(id+"F0.wireOp",EDGE,"E7.filletArc"),sQuery(id+"F0.wireOp",EDGE,"E8.trimOffspring"),sQuery(id+"F0.wireOp",EDGE,"E9.MirrorCS"),sQuery(id+"F0.wireOp",EDGE,"E10.MirrorCS"),sQuery(id+"F0.wireOp",EDGE,"E11.MirrorCS"),sQuery(id+"F0.wireOp",EDGE,"E12.MirrorCS"),sQuery(id+"F0.wireOp",EDGE,"E13.MirrorCS"),sQuery(id+"F0.wireOp",EDGE,"E14.MirrorCS"),sQuery(id+"F0.wireOp",EDGE,"E15.MirrorCS"),sQuery(id+"F0.wireOp",EDGE,"E16.MirrorCS"),sQuery(id+"F0.wireOp",EDGE,"E17.MirrorCS"),sQuery(id+"F0.wireOp",EDGE,"E18.MirrorCS"),sQuery(id+"F0.wireOp",EDGE,"E19.MirrorCS"),sQuery(id+"F0.wireOp",EDGE,"E20.MirrorCS"),sQuery(id+"F0.wireOp",EDGE,"E21.MirrorCS"),subQ5,sQuery(id+"F0.wireOp",EDGE,"E23.MirrorCS"),subQ4,sQuery(id+"F0.wireOp",EDGE,"E25.MirrorCS"),sQuery(id+"F0.wireOp",EDGE,"E26.MirrorCS"),sQuery(id+"F0.wireOp",EDGE,"E27.MirrorCS"),sQuery(id+"F0.wireOp",EDGE,"E28.MirrorCS"),sQuery(id+"F0.wireOp",EDGE,"E29.MirrorCS"),sQuery(id+"F0.wireOp",EDGE,"E30.MirrorCS"),sQuery(id+"F0.wireOp",EDGE,"E31.MirrorCS"),sQuery(id+"F0.wireOp",EDGE,"E32.MirrorCS"),sQuery(id+"F0.wireOp",EDGE,"E33.MirrorCS"),sQuery(id+"F0.wireOp",EDGE,"E34.MirrorCS"),sQuery(id+"F0.wireOp",EDGE,"E35.MirrorCS"),subQ7,subQ8,sQuery(id+"F0.wireOp",EDGE,"E38"),subQ9])],"isStart":false})});}
            var Q24;
            {var subQ1=sQuery(id+"F0.wireOp",EDGE,"E25.MirrorCS");var subQ5=sQuery(id+"F0.wireOp",EDGE,"E34.MirrorCS");var subQ6=sQuery(id+"F0.wireOp",EDGE,"E36");var subQ7=sQuery(id+"F0.wireOp",EDGE,"E38");var subQ8=sQuery(id+"F0.wireOp",EDGE,"E15.MirrorCS");var subQ9=sQuery(id+"F0.wireOp",EDGE,"E16.MirrorCS");var subQ10=sQuery(id+"F0.wireOp",EDGE,"E39");Q24=makeQuery(id+"F13.opBoolean","SPLIT",FACE,{"disambiguationData":[TD([makeQuery(id+"F1.opExtrude","SWEPT_FACE",FACE,{"disambiguationData":[OSD([subQ8])]})])],"derivedFrom":makeQuery(id+"F1.opExtrude","CAP_FACE",FACE,{"disambiguationData":[OSD([sQuery(id+"F0.wireOp",EDGE,"E0.left"),sQuery(id+"F0.wireOp",EDGE,"E1"),sQuery(id+"F0.wireOp",EDGE,"E2"),sQuery(id+"F0.wireOp",EDGE,"E3"),sQuery(id+"F0.wireOp",EDGE,"E4"),sQuery(id+"F0.wireOp",EDGE,"E5"),sQuery(id+"F0.wireOp",EDGE,"E6.filletArc"),sQuery(id+"F0.wireOp",EDGE,"E7.filletArc"),sQuery(id+"F0.wireOp",EDGE,"E8.trimOffspring"),sQuery(id+"F0.wireOp",EDGE,"E9.MirrorCS"),sQuery(id+"F0.wireOp",EDGE,"E10.MirrorCS"),sQuery(id+"F0.wireOp",EDGE,"E11.MirrorCS"),sQuery(id+"F0.wireOp",EDGE,"E12.MirrorCS"),sQuery(id+"F0.wireOp",EDGE,"E13.MirrorCS"),sQuery(id+"F0.wireOp",EDGE,"E14.MirrorCS"),subQ8,subQ9,sQuery(id+"F0.wireOp",EDGE,"E17.MirrorCS"),sQuery(id+"F0.wireOp",EDGE,"E18.MirrorCS"),sQuery(id+"F0.wireOp",EDGE,"E19.MirrorCS"),sQuery(id+"F0.wireOp",EDGE,"E20.MirrorCS"),sQuery(id+"F0.wireOp",EDGE,"E21.MirrorCS"),sQuery(id+"F0.wireOp",EDGE,"E22.MirrorCS"),sQuery(id+"F0.wireOp",EDGE,"E23.MirrorCS"),sQuery(id+"F0.wireOp",EDGE,"E24.MirrorCS"),subQ1,sQuery(id+"F0.wireOp",EDGE,"E26.MirrorCS"),sQuery(id+"F0.wireOp",EDGE,"E27.MirrorCS"),sQuery(id+"F0.wireOp",EDGE,"E28.MirrorCS"),sQuery(id+"F0.wireOp",EDGE,"E29.MirrorCS"),sQuery(id+"F0.wireOp",EDGE,"E30.MirrorCS"),sQuery(id+"F0.wireOp",EDGE,"E31.MirrorCS"),sQuery(id+"F0.wireOp",EDGE,"E32.MirrorCS"),sQuery(id+"F0.wireOp",EDGE,"E33.MirrorCS"),subQ5,sQuery(id+"F0.wireOp",EDGE,"E35.MirrorCS"),subQ6,sQuery(id+"F0.wireOp",EDGE,"E37"),subQ7,subQ10])],"isStart":false})});}
            var Q25;
            {var subQ0=sQuery(id+"F7.wireOp",EDGE,"E83");Q25=makeQuery(id+"F13.opBoolean","SPLIT",FACE,{"disambiguationData":[TD([makeQuery(id+"F4iPU1aoNzSSLv7_1.1.F8.opExtrude","SWEPT_FACE",FACE,{"disambiguationData":[OSD([subQ0])]})])],"derivedFrom":makeQuery(id+"F4iPU1aoNzSSLv7_1.1.F8.opExtrude","CAP_FACE",FACE,{"disambiguationData":[OSD([sQuery(id+"F7.wireOp",EDGE,"E82"),subQ0,sQuery(id+"F7.wireOp",EDGE,"E84.0"),sQuery(id+"F7.wireOp",EDGE,"E85.0")])],"isStart":false})});}
            var Q26;
            Q26=makeQuery(id+"F10.opExtrude","SWEPT_EDGE",EDGE,{"disambiguationData":[OSD([sQuery(id+"F0.wireOp",EDGE,"E36"),sQuery(id+"F9.wireOp",EDGE,"E86.right"),sQuery(id+"F9.wireOp",EDGE,"E88")])]});
            var Q27;
            Q27=makeQuery(id+"F4iPU1aoNzSSLv7_1.1.F8.opExtrude","SWEPT_EDGE",EDGE,{"disambiguationData":[OSD([sQuery(id+"F7.wireOp",EDGE,"E83"),sQuery(id+"F7.wireOp",EDGE,"E84.0")])]});
            var Q28;
            Q28=makeQuery(id+"F4iPU1aoNzSSLv7_1.1.F8.opExtrude","CAP_EDGE",EDGE,{"disambiguationData":[OSD([sQuery(id+"F7.wireOp",EDGE,"E83")])],"isStart":true});
            var Q29;
            Q29=makeQuery(id+"F4iPU1aoNzSSLv7_1.1.F8.opExtrude","CAP_EDGE",EDGE,{"disambiguationData":[OSD([sQuery(id+"F7.wireOp",EDGE,"E83")])],"isStart":false});
            var Q30;
            Q30=makeQuery(id+"F12.boolean.opBoolean","INTERSECT",EDGE,{"derivedFrom":[makeQuery(id+"F10.opExtrude","CAP_FACE",FACE,{"disambiguationData":[OSD([sQuery(id+"F5.wireOp",EDGE,"E80")])],"isStart":false}),makeQuery(id+"F12.opExtrude","SWEPT_FACE",FACE,{"disambiguationData":[OSD([sQuery(id+"F11.wireOp",EDGE,"E89.MirrorCS")])]})]});
            var Q31;
            {var subQ0=sQuery(id+"F7.wireOp",EDGE,"E84.0");var subQ1=sQuery(id+"F7.wireOp",EDGE,"E83");Q31=makeQuery(id+"F13.opBoolean","SPLIT",EDGE,{"disambiguationData":[TD([makeQuery(id+"F4iPU1aoNzSSLv7_1.1.F8.opExtrude","SWEPT_FACE",FACE,{"disambiguationData":[OSD([subQ1])]})])],"derivedFrom":makeQuery(id+"F4iPU1aoNzSSLv7_1.1.F8.opExtrude","CAP_EDGE",EDGE,{"disambiguationData":[OSD([subQ0])],"isStart":true})});}
            var Q32;
            Q32=makeQuery(id+"F10.opExtrude","TWEAK_EDGE",EDGE,{"derivedFrom":[makeQuery(id+"F6.opExtrude","SWEPT_FACE",FACE,{"disambiguationData":[OSD([sQuery(id+"F5.wireOp",EDGE,"E80")])]}),makeQuery(id+"F9.imprint","IMPRINT",EDGE,{"derivedFrom":sQuery(id+"F9.wireOp",EDGE,"E87")})]});
            var Q33;
            Q33=makeQuery(id+"F8.opExtrude","SWEPT_EDGE",EDGE,{"disambiguationData":[OSD([sQuery(id+"F7.wireOp",EDGE,"E83"),sQuery(id+"F7.wireOp",EDGE,"E84.0")])]});
            fillet(context, id + "F15", {"entities" : qUnion([Q0, Q1, Q2, Q3, Q4, Q5, Q6, Q7, Q8, Q9, Q10, Q11, Q12, Q13, Q14, Q15, Q16, Q17, Q18, Q19, Q20, Q21, Q22, Q23, Q24, Q25, Q26, Q27, Q28, Q29, Q30, Q31, Q32, Q33]), "radius" : 3.05 * mm, "tangentPropagation" : true, "allowEdgeOverflow" : false});
        }
        {
            var Q0;
            Q0=qCreatedBy(makeId("Top.planeOp"),FACE);
            cPlane(context, id + "F16", {"entities" : qUnion([Q0]), "cplaneType" : CPlaneType.OFFSET, "offset" : 138.11 * mm, "width" : 152.4 * mm, "height" : 152.4 * mm});
        }
        {
            var Q0;
            Q0=qCreatedBy(id+"F16.planeOp",FACE);
            var sketch = newSketch(context, id + "F17", { "sketchPlane" : qUnion([Q0])});
            skPoint(sketch, "E95", {"position": v(0, -85.73) * mm});
            skPoint(sketch, "E96", {"position": v(0, 85.73) * mm});
            skSolve(sketch);
        }
        {
            var Q0;
            Q0=sQuery(id+"F17.wireOp",VERTEX,"E95");
            var Q1;
            Q1=sQuery(id+"F17.wireOp",VERTEX,"E96");
            var Q2;
            Q2=makeQuery(id+"F10.opExtrude","SWEPT_BODY",BODY,{"disambiguationData":[OSD([sQuery(id+"F9.wireOp",EDGE,"E86.left"),sQuery(id+"F9.wireOp",EDGE,"E86.right"),sQuery(id+"F9.wireOp",EDGE,"E87"),sQuery(id+"F9.wireOp",EDGE,"E88")])]});
            hole(context, id + "F18", {"style" : HoleStyle.SIMPLE, "endStyle" : HoleEndStyle.BLIND, "standardTappedOrClearance" : lookupTablePath({ "standard" : "ISO", "fit" : "Normal", "size" : "M5", "type" : "Clearance" }), "standardBlindInLast" : lookupTablePath({ "fit" : "Standard", "standard" : "ISO", "size" : "M5", "type" : "Clearance" }), "holeDiameter" : 5.5 * mm, "holeDepth" : 25.4 * mm, "tappedDepth" : 25.4 * mm, "tapClearance" : 0, "locations" : qUnion([Q0, Q1]), "scope" : qUnion([Q2])});
        }
        {
            var Q0;
            Q0=makeQuery(id+"F6.opExtrude","CAP_EDGE",EDGE,{"disambiguationData":[OSD([sQuery(id+"F5.wireOp",EDGE,"E81")])],"isStart":false});
            var Q1;
            Q1=makeQuery(id+"F4iPU1aoNzSSLv7_1.1.F6.opExtrude","CAP_EDGE",EDGE,{"disambiguationData":[OSD([sQuery(id+"F5.wireOp",EDGE,"E81")])],"isStart":true});
            var Q2;
            Q2=makeQuery(id+"F4iPU1aoNzSSLv7_1.1.F6.opExtrude","CAP_EDGE",EDGE,{"disambiguationData":[OSD([sQuery(id+"F5.wireOp",EDGE,"E81")])],"isStart":false});
            var Q3;
            Q3=makeQuery(id+"F6.opExtrude","CAP_EDGE",EDGE,{"disambiguationData":[OSD([sQuery(id+"F5.wireOp",EDGE,"E81")])],"isStart":true});
            chamfer(context, id + "F19", {"entities" : qUnion([Q0, Q1, Q2, Q3]), "width" : 0.76 * mm, "tangentPropagation" : true});
        }
    });
